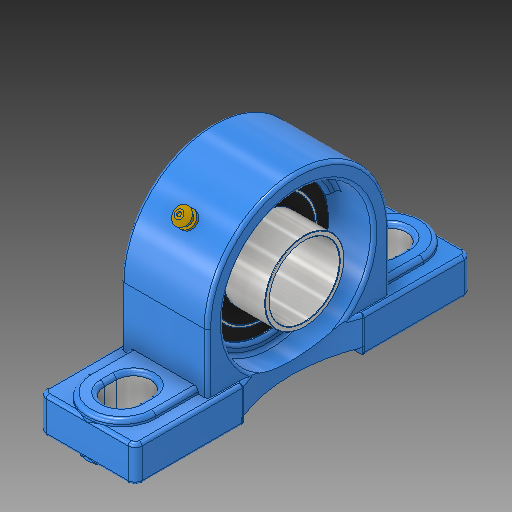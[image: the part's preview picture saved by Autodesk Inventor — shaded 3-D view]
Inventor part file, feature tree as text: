
AUTODESK INVENTOR PART (.ipt)
format: ipt  version: 2019 (Build 230136000, 136)  size: 667,648 bytes
history: native  units: in
note: dims shown in document units (in); Inventor stores cm internally (conversion verified against a paired STEP export)
features: sketch x28, plane x7, other x3
ambient origin geometry x8: Origin, YZ Plane, XZ Plane, XY Plane, X Axis, Y Axis, Z Axis, Center Point
bodies: Solid1 (feature_tree)
feature tree (38):
  other  "Pillow Bearing inventor.ipt"
  other  "Solid1::Pillow Bearing inventor.ipt"
  other  "TaggingFeature1"
  sketch  "Sketch1"  dims[d0=0.3937in]
  sketch  "Sketch2"
  sketch  "Sketch3"
  sketch  "Sketch4"
  sketch  "Sketch5"
  sketch  "Sketch6"
  sketch  "Sketch7"
  sketch  "Sketch8"
  sketch  "Sketch9"
  sketch  "Sketch10"
  sketch  "Sketch11"
  sketch  "Sketch13"
  sketch  "Sketch14"
  sketch  "Sketch15"
  sketch  "Sketch17"
  sketch  "Sketch18"
  sketch  "Sketch19"
  sketch  "Sketch20"
  sketch  "Sketch21"
  sketch  "Sketch22"
  sketch  "Sketch23"
  sketch  "Sketch24"
  sketch  "Sketch25"
  sketch  "Sketch26"
  sketch  "Sketch27"
  sketch  "Sketch28"
  sketch  "Sketch29"
  sketch  "Sketch30"
  plane  "Work Plane1"
  plane  "Work Plane2"
  plane  "Work Plane5"
  plane  "Work Plane6"
  plane  "Work Plane7"
  plane  "Work Plane8"
  plane  "Work Plane9"
